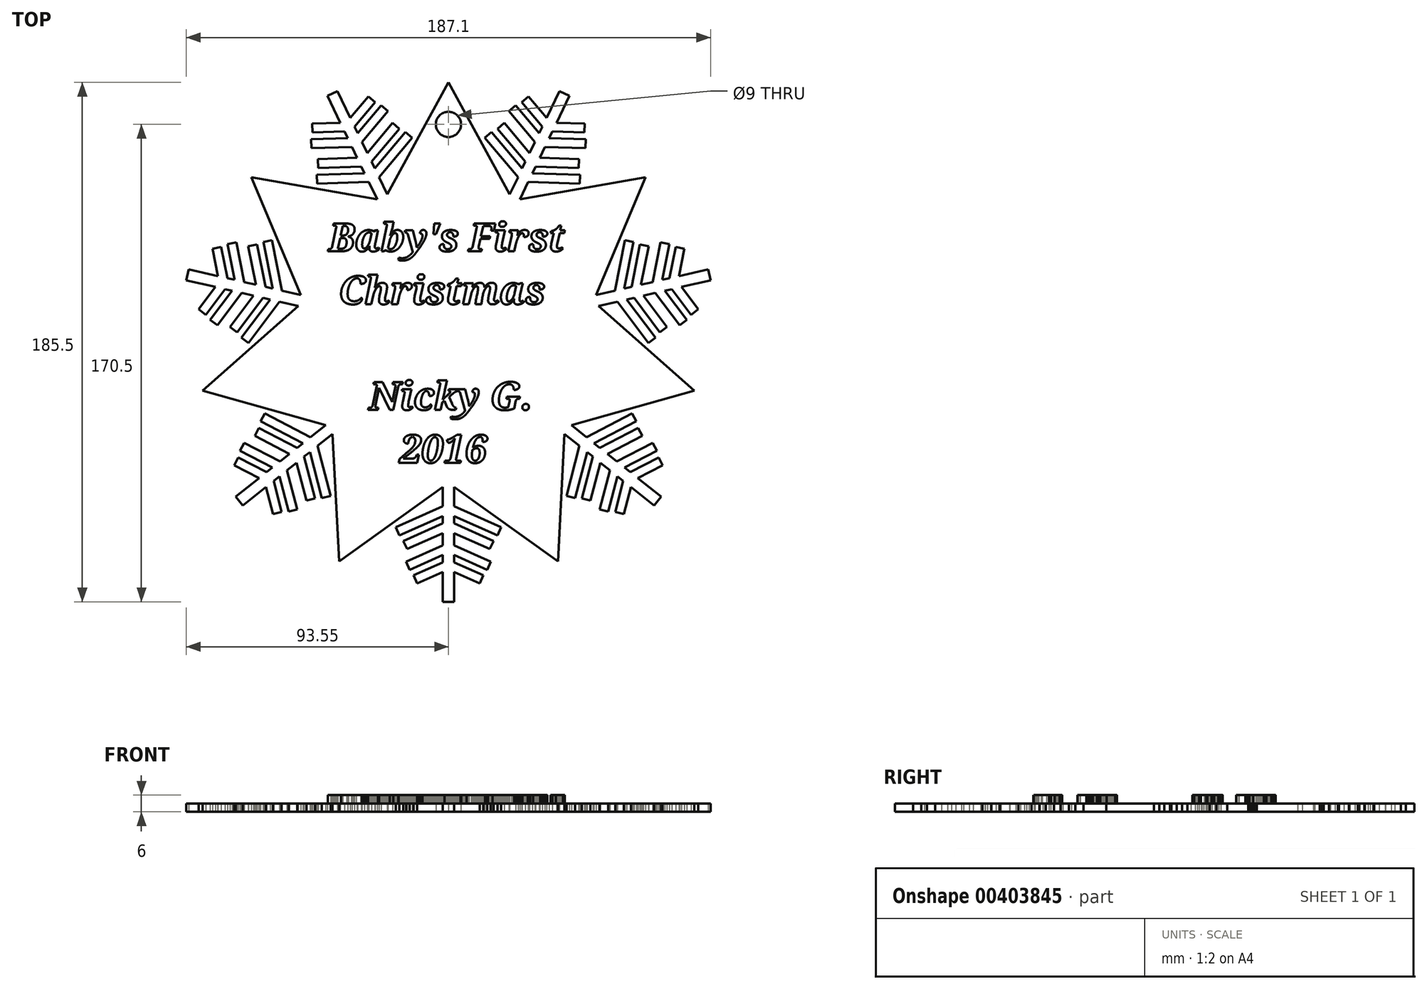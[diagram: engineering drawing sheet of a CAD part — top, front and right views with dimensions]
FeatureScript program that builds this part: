
annotation { "Feature Type Name" : "Feature", "Feature Type Description" : "" }
export const myFeature = defineFeature(function(context is Context, id is Id, definition is map)
    precondition{}
    {
        {
            var Q0;
            Q0=qCreatedBy(makeId("Top.planeOp"),FACE);
            var sketch = newSketch(context, id + "F0", { "sketchPlane" : qUnion([Q0])});
            skLineSegment(sketch, "E0.0", {"start": v(-21.86, 50) * mm, "end": v(21.86, 50) * mm});
            skLineSegment(sketch, "E0.1", {"start": v(25.46, 48.26) * mm, "end": v(52.72, 14.08) * mm});
            skLineSegment(sketch, "E0.2", {"start": v(53.61, 10.18) * mm, "end": v(43.88, -32.44) * mm});
            skLineSegment(sketch, "E0.3", {"start": v(41.39, -35.56) * mm, "end": v(2, -54.53) * mm});
            skLineSegment(sketch, "E0.4", {"start": v(-2, -54.53) * mm, "end": v(-41.39, -35.56) * mm});
            skLineSegment(sketch, "E0.5", {"start": v(-43.88, -32.44) * mm, "end": v(-53.61, 10.18) * mm});
            skLineSegment(sketch, "E0.6", {"start": v(-52.72, 14.08) * mm, "end": v(-25.46, 48.26) * mm});
            skPoint(sketch, "E0.0.midPoint", {"position": v(0, 50) * mm});
            skLineSegment(sketch, "E1", {"start": v(0, 0) * mm, "end": v(24.08, 50) * mm, "construction": true});
            skLineSegment(sketch, "E2", {"start": v(0, 0) * mm, "end": v(-24.08, 50) * mm, "construction": true});
            skLineSegment(sketch, "E3", {"start": v(0, 0) * mm, "end": v(-54.1, 12.35) * mm, "construction": true});
            skLineSegment(sketch, "E4", {"start": v(0, 0) * mm, "end": v(-43.39, -34.6) * mm, "construction": true});
            skLineSegment(sketch, "E5", {"start": v(0, 0) * mm, "end": v(0, -55.5) * mm, "construction": true});
            skLineSegment(sketch, "E6", {"start": v(0, 0) * mm, "end": v(43.39, -34.6) * mm, "construction": true});
            skLineSegment(sketch, "E7", {"start": v(0, 0) * mm, "end": v(54.1, 12.35) * mm, "construction": true});
            skLineSegment(sketch, "E8", {"start": v(-24.08, 50) * mm, "end": v(-41.43, 86.04) * mm, "construction": true});
            skLineSegment(sketch, "E9", {"start": v(24.08, 50) * mm, "end": v(41.43, 86.04) * mm, "construction": true});
            skLineSegment(sketch, "E10", {"start": v(54.1, 12.35) * mm, "end": v(93.1, 21.25) * mm, "construction": true});
            skLineSegment(sketch, "E11", {"start": v(43.39, -34.6) * mm, "end": v(74.66, -59.54) * mm, "construction": true});
            skLineSegment(sketch, "E12", {"start": v(0, -55.5) * mm, "end": v(0, -95.5) * mm, "construction": true});
            skLineSegment(sketch, "E13", {"start": v(-43.39, -34.6) * mm, "end": v(-74.66, -59.54) * mm, "construction": true});
            skLineSegment(sketch, "E14.0", {"start": v(-25.88, 49.13) * mm, "end": v(-28.43, 54.43) * mm});
            skLineSegment(sketch, "E15.0", {"start": v(25.88, 49.13) * mm, "end": v(28.43, 54.43) * mm});
            skLineSegment(sketch, "E16.0", {"start": v(54.55, 10.4) * mm, "end": v(60.28, 11.7) * mm});
            skLineSegment(sketch, "E17.0", {"start": v(53.66, 14.3) * mm, "end": v(59.39, 15.6) * mm});
            skLineSegment(sketch, "E18.0", {"start": v(42.14, -36.16) * mm, "end": v(46.74, -39.83) * mm});
            skLineSegment(sketch, "E19.0", {"start": v(44.64, -33.04) * mm, "end": v(49.23, -36.7) * mm});
            skLineSegment(sketch, "E20.0", {"start": v(2, -55.5) * mm, "end": v(2, -61.37) * mm});
            skLineSegment(sketch, "E21.0", {"start": v(-2, -55.5) * mm, "end": v(-2, -61.37) * mm});
            skLineSegment(sketch, "E22.0", {"start": v(-44.64, -33.04) * mm, "end": v(-49.23, -36.7) * mm});
            skLineSegment(sketch, "E23.0", {"start": v(-42.14, -36.16) * mm, "end": v(-46.74, -39.83) * mm});
            skLineSegment(sketch, "E24.0", {"start": v(-53.66, 14.3) * mm, "end": v(-59.39, 15.6) * mm});
            skLineSegment(sketch, "E25.0", {"start": v(-54.55, 10.4) * mm, "end": v(-60.28, 11.7) * mm});
            skLineSegment(sketch, "E26", {"start": v(-22.28, 50.87) * mm, "end": v(-21.86, 50) * mm});
            skLineSegment(sketch, "E27", {"start": v(-25.88, 49.13) * mm, "end": v(-25.46, 48.26) * mm});
            skLineSegment(sketch, "E28", {"start": v(-53.66, 14.3) * mm, "end": v(-52.72, 14.08) * mm});
            skLineSegment(sketch, "E29", {"start": v(-54.55, 10.4) * mm, "end": v(-53.61, 10.18) * mm});
            skLineSegment(sketch, "E30", {"start": v(-44.64, -33.04) * mm, "end": v(-43.88, -32.44) * mm});
            skLineSegment(sketch, "E31", {"start": v(-42.14, -36.16) * mm, "end": v(-41.39, -35.56) * mm});
            skLineSegment(sketch, "E32", {"start": v(-2, -55.5) * mm, "end": v(-2, -54.53) * mm});
            skLineSegment(sketch, "E33", {"start": v(2, -55.5) * mm, "end": v(2, -54.53) * mm});
            skLineSegment(sketch, "E34", {"start": v(42.14, -36.16) * mm, "end": v(41.39, -35.56) * mm});
            skLineSegment(sketch, "E35", {"start": v(44.64, -33.04) * mm, "end": v(43.88, -32.44) * mm});
            skLineSegment(sketch, "E36", {"start": v(54.55, 10.4) * mm, "end": v(53.61, 10.18) * mm});
            skLineSegment(sketch, "E37", {"start": v(53.66, 14.3) * mm, "end": v(52.72, 14.08) * mm});
            skLineSegment(sketch, "E38", {"start": v(22.28, 50.87) * mm, "end": v(21.86, 50) * mm});
            skLineSegment(sketch, "E39", {"start": v(25.88, 49.13) * mm, "end": v(25.46, 48.26) * mm});
            skLineSegment(sketch, "E40", {"start": v(-43.24, 85.17) * mm, "end": v(-39.63, 86.9) * mm});
            skLineSegment(sketch, "E41", {"start": v(43.24, 85.17) * mm, "end": v(39.63, 86.9) * mm});
            skLineSegment(sketch, "E42", {"start": v(93.55, 19.3) * mm, "end": v(92.66, 23.2) * mm});
            skLineSegment(sketch, "E43", {"start": v(73.41, -61.1) * mm, "end": v(75.9, -57.98) * mm});
            skLineSegment(sketch, "E44", {"start": v(2, -95.5) * mm, "end": v(-2, -95.5) * mm});
            skLineSegment(sketch, "E45", {"start": v(-73.41, -61.1) * mm, "end": v(-75.9, -57.98) * mm});
            skLineSegment(sketch, "E46", {"start": v(-93.55, 19.3) * mm, "end": v(-92.66, 23.2) * mm});
            skPoint(sketch, "E47.6.1", {"position": v(-40.06, 76.4) * mm});
            skPoint(sketch, "E47.6.2", {"position": v(-39.8, 73.96) * mm});
            skPoint(sketch, "E47.6.14", {"position": v(-34.76, 78.96) * mm});
            skPoint(sketch, "E47.6.19", {"position": v(-33.01, 77.23) * mm});
            skPoint(sketch, "E47.center", {"position": v(0, 0) * mm});
            skLineSegment(sketch, "E48.trimOffspring", {"start": v(-82.3, 20.84) * mm, "end": v(-92.66, 23.2) * mm});
            skLineSegment(sketch, "E49.trimOffspring", {"start": v(-76.35, 19.48) * mm, "end": v(-78.9, 20.06) * mm});
            skLineSegment(sketch, "E50.trimOffspring", {"start": v(-68.74, 17.74) * mm, "end": v(-72.95, 18.7) * mm});
            skLineSegment(sketch, "E51.trimOffspring", {"start": v(-62.79, 16.38) * mm, "end": v(-65.34, 16.96) * mm});
            skLineSegment(sketch, "E52.trimOffspring", {"start": v(-63.68, 12.48) * mm, "end": v(-66.23, 13.06) * mm});
            skLineSegment(sketch, "E53.trimOffspring", {"start": v(-69.63, 13.84) * mm, "end": v(-73.84, 14.8) * mm});
            skLineSegment(sketch, "E54.trimOffspring", {"start": v(-83.2, 16.94) * mm, "end": v(-93.55, 19.3) * mm});
            skLineSegment(sketch, "E55.trimOffspring", {"start": v(-77.24, 15.58) * mm, "end": v(-79.8, 16.16) * mm});
            skLineSegment(sketch, "E56.trimOffspring", {"start": v(-26.34, 59.3) * mm, "end": v(-27.47, 61.66) * mm});
            skLineSegment(sketch, "E57.trimOffspring", {"start": v(-29.94, 57.57) * mm, "end": v(-31.08, 59.93) * mm});
            skLineSegment(sketch, "E58.trimOffspring", {"start": v(-35.98, 70.1) * mm, "end": v(-37.11, 72.46) * mm});
            skLineSegment(sketch, "E59.trimOffspring", {"start": v(-35.02, 77.34) * mm, "end": v(-39.63, 86.9) * mm});
            skLineSegment(sketch, "E60.trimOffspring", {"start": v(-32.38, 71.84) * mm, "end": v(-33.51, 74.2) * mm});
            skLineSegment(sketch, "E61.trimOffspring", {"start": v(-28.99, 64.8) * mm, "end": v(-30.86, 68.7) * mm});
            skLineSegment(sketch, "E62.trimOffspring", {"start": v(-38.63, 75.6) * mm, "end": v(-43.24, 85.17) * mm});
            skLineSegment(sketch, "E63.trimOffspring", {"start": v(29.94, 57.57) * mm, "end": v(31.08, 59.93) * mm});
            skLineSegment(sketch, "E64.trimOffspring", {"start": v(26.34, 59.3) * mm, "end": v(27.47, 61.66) * mm});
            skLineSegment(sketch, "E65.trimOffspring", {"start": v(28.99, 64.8) * mm, "end": v(30.86, 68.7) * mm});
            skLineSegment(sketch, "E66.trimOffspring", {"start": v(32.38, 71.84) * mm, "end": v(33.51, 74.2) * mm});
            skLineSegment(sketch, "E67.trimOffspring", {"start": v(35.98, 70.1) * mm, "end": v(37.11, 72.46) * mm});
            skLineSegment(sketch, "E68.trimOffspring", {"start": v(35.02, 77.34) * mm, "end": v(39.63, 86.9) * mm});
            skLineSegment(sketch, "E69.trimOffspring", {"start": v(38.63, 75.6) * mm, "end": v(43.24, 85.17) * mm});
            skLineSegment(sketch, "E70.trimOffspring", {"start": v(63.68, 12.48) * mm, "end": v(66.23, 13.06) * mm});
            skLineSegment(sketch, "E71.trimOffspring", {"start": v(62.79, 16.38) * mm, "end": v(65.34, 16.96) * mm});
            skLineSegment(sketch, "E72.trimOffspring", {"start": v(69.63, 13.84) * mm, "end": v(73.84, 14.8) * mm});
            skLineSegment(sketch, "E73.trimOffspring", {"start": v(68.74, 17.74) * mm, "end": v(72.95, 18.7) * mm});
            skLineSegment(sketch, "E74.trimOffspring", {"start": v(77.24, 15.58) * mm, "end": v(79.8, 16.16) * mm});
            skLineSegment(sketch, "E75.trimOffspring", {"start": v(76.35, 19.48) * mm, "end": v(78.9, 20.06) * mm});
            skLineSegment(sketch, "E76.trimOffspring", {"start": v(82.3, 20.84) * mm, "end": v(92.66, 23.2) * mm});
            skLineSegment(sketch, "E77.trimOffspring", {"start": v(83.2, 16.94) * mm, "end": v(93.55, 19.3) * mm});
            skLineSegment(sketch, "E78.trimOffspring", {"start": v(65.1, -54.48) * mm, "end": v(73.41, -61.1) * mm});
            skLineSegment(sketch, "E79.trimOffspring", {"start": v(67.6, -51.35) * mm, "end": v(75.9, -57.98) * mm});
            skLineSegment(sketch, "E80.trimOffspring", {"start": v(62.83, -47.55) * mm, "end": v(64.88, -49.18) * mm});
            skLineSegment(sketch, "E81.trimOffspring", {"start": v(60.34, -50.68) * mm, "end": v(62.38, -52.3) * mm});
            skLineSegment(sketch, "E82.trimOffspring", {"start": v(54.23, -45.8) * mm, "end": v(57.61, -48.5) * mm});
            skLineSegment(sketch, "E83.trimOffspring", {"start": v(56.73, -42.68) * mm, "end": v(60.1, -45.38) * mm});
            skLineSegment(sketch, "E84.trimOffspring", {"start": v(51.96, -38.88) * mm, "end": v(54, -40.5) * mm});
            skLineSegment(sketch, "E85.trimOffspring", {"start": v(49.46, -42) * mm, "end": v(51.5, -43.63) * mm});
            skLineSegment(sketch, "E86.trimOffspring", {"start": v(-2, -84.87) * mm, "end": v(-2, -95.5) * mm});
            skLineSegment(sketch, "E87.trimOffspring", {"start": v(2, -84.87) * mm, "end": v(2, -95.5) * mm});
            skLineSegment(sketch, "E88.trimOffspring", {"start": v(2, -78.77) * mm, "end": v(2, -81.39) * mm});
            skLineSegment(sketch, "E89.trimOffspring", {"start": v(-2, -78.77) * mm, "end": v(-2, -81.39) * mm});
            skLineSegment(sketch, "E90.trimOffspring", {"start": v(-2, -70.96) * mm, "end": v(-2, -75.28) * mm});
            skLineSegment(sketch, "E91.trimOffspring", {"start": v(2, -70.96) * mm, "end": v(2, -75.28) * mm});
            skLineSegment(sketch, "E92.trimOffspring", {"start": v(2, -64.86) * mm, "end": v(2, -67.48) * mm});
            skLineSegment(sketch, "E93.trimOffspring", {"start": v(-2, -64.86) * mm, "end": v(-2, -67.48) * mm});
            skLineSegment(sketch, "E94.trimOffspring", {"start": v(-67.6, -51.35) * mm, "end": v(-75.9, -57.98) * mm});
            skLineSegment(sketch, "E95.trimOffspring", {"start": v(-65.1, -54.48) * mm, "end": v(-73.41, -61.1) * mm});
            skLineSegment(sketch, "E96.trimOffspring", {"start": v(-60.34, -50.68) * mm, "end": v(-62.38, -52.3) * mm});
            skLineSegment(sketch, "E97.trimOffspring", {"start": v(-62.83, -47.55) * mm, "end": v(-64.88, -49.18) * mm});
            skLineSegment(sketch, "E98.trimOffspring", {"start": v(-56.73, -42.68) * mm, "end": v(-60.1, -45.38) * mm});
            skLineSegment(sketch, "E99.trimOffspring", {"start": v(-54.23, -45.8) * mm, "end": v(-57.61, -48.5) * mm});
            skLineSegment(sketch, "E100.trimOffspring", {"start": v(-49.46, -42) * mm, "end": v(-51.5, -43.63) * mm});
            skLineSegment(sketch, "E101.trimOffspring", {"start": v(-51.96, -38.88) * mm, "end": v(-54, -40.5) * mm});
            skLineSegment(sketch, "E102", {"start": v(-24.83, 56.16) * mm, "end": v(-22.28, 50.87) * mm});
            skLineSegment(sketch, "E103", {"start": v(24.83, 56.16) * mm, "end": v(22.28, 50.87) * mm});
            skLineSegment(sketch, "E104", {"start": v(-34.47, 66.96) * mm, "end": v(-32.6, 63.07) * mm});
            skLineSegment(sketch, "E105", {"start": v(34.47, 66.96) * mm, "end": v(32.6, 63.07) * mm});
            skLineSegment(sketch, "E106", {"start": v(79.8, 16.16) * mm, "end": v(86.64, 7.02) * mm});
            skLineSegment(sketch, "E107", {"start": v(83.2, 16.94) * mm, "end": v(89.19, 8.93) * mm});
            skLineSegment(sketch, "E108", {"start": v(86.64, 7.02) * mm, "end": v(89.19, 8.93) * mm});
            skLineSegment(sketch, "E109", {"start": v(77.24, 15.58) * mm, "end": v(85.04, 5.18) * mm});
            skLineSegment(sketch, "E110", {"start": v(73.84, 14.8) * mm, "end": v(82.5, 3.27) * mm});
            skLineSegment(sketch, "E111", {"start": v(85.04, 5.18) * mm, "end": v(82.5, 3.27) * mm});
            skLineSegment(sketch, "E112", {"start": v(69.63, 13.84) * mm, "end": v(78.03, 2.64) * mm});
            skLineSegment(sketch, "E113", {"start": v(66.23, 13.06) * mm, "end": v(75.48, 0.73) * mm});
            skLineSegment(sketch, "E114", {"start": v(78.03, 2.64) * mm, "end": v(75.48, 0.73) * mm});
            skLineSegment(sketch, "E115", {"start": v(63.68, 12.48) * mm, "end": v(73.88, -1.12) * mm});
            skLineSegment(sketch, "E116", {"start": v(60.28, 11.7) * mm, "end": v(71.33, -3.03) * mm});
            skLineSegment(sketch, "E117", {"start": v(73.88, -1.12) * mm, "end": v(71.33, -3.03) * mm});
            skLineSegment(sketch, "E118.MirrorCS", {"start": v(71.44, 31.48) * mm, "end": v(68.32, 32.1) * mm});
            skLineSegment(sketch, "E119.MirrorCS", {"start": v(59.39, 15.6) * mm, "end": v(62.95, 33.68) * mm});
            skLineSegment(sketch, "E120.MirrorCS", {"start": v(66.07, 33.06) * mm, "end": v(62.95, 33.68) * mm});
            skLineSegment(sketch, "E121.MirrorCS", {"start": v(62.79, 16.38) * mm, "end": v(66.07, 33.06) * mm});
            skLineSegment(sketch, "E122.MirrorCS", {"start": v(65.34, 16.96) * mm, "end": v(68.32, 32.1) * mm});
            skLineSegment(sketch, "E123.MirrorCS", {"start": v(68.74, 17.74) * mm, "end": v(71.44, 31.48) * mm});
            skLineSegment(sketch, "E124.MirrorCS", {"start": v(72.95, 18.7) * mm, "end": v(75.74, 32.85) * mm});
            skLineSegment(sketch, "E125.MirrorCS", {"start": v(78.86, 32.23) * mm, "end": v(75.74, 32.85) * mm});
            skLineSegment(sketch, "E126.MirrorCS", {"start": v(76.35, 19.48) * mm, "end": v(78.86, 32.23) * mm});
            skLineSegment(sketch, "E127.MirrorCS", {"start": v(78.9, 20.06) * mm, "end": v(81.1, 31.26) * mm});
            skLineSegment(sketch, "E128.MirrorCS", {"start": v(82.3, 20.84) * mm, "end": v(84.23, 30.65) * mm});
            skLineSegment(sketch, "E129.MirrorCS", {"start": v(81.1, 31.26) * mm, "end": v(84.23, 30.65) * mm});
            skLineSegment(sketch, "E130.1.0", {"start": v(48.53, 72.12) * mm, "end": v(48.62, 75.3) * mm});
            skLineSegment(sketch, "E130.1.1", {"start": v(38.63, 75.6) * mm, "end": v(48.62, 75.3) * mm});
            skLineSegment(sketch, "E130.1.2", {"start": v(37.11, 72.46) * mm, "end": v(48.53, 72.12) * mm});
            skLineSegment(sketch, "E130.1.3", {"start": v(35.98, 70.1) * mm, "end": v(48.97, 69.71) * mm});
            skLineSegment(sketch, "E130.1.4", {"start": v(48.97, 69.71) * mm, "end": v(48.88, 66.53) * mm});
            skLineSegment(sketch, "E130.1.5", {"start": v(34.47, 66.96) * mm, "end": v(48.88, 66.53) * mm});
            skLineSegment(sketch, "E130.1.6", {"start": v(32.6, 63.07) * mm, "end": v(46.59, 62.65) * mm});
            skLineSegment(sketch, "E130.1.7", {"start": v(46.59, 62.65) * mm, "end": v(46.49, 59.46) * mm});
            skLineSegment(sketch, "E130.1.8", {"start": v(31.08, 59.93) * mm, "end": v(46.49, 59.46) * mm});
            skLineSegment(sketch, "E130.1.9", {"start": v(29.94, 57.57) * mm, "end": v(46.94, 57.06) * mm});
            skLineSegment(sketch, "E130.1.10", {"start": v(46.94, 57.06) * mm, "end": v(46.84, 53.88) * mm});
            skLineSegment(sketch, "E130.1.11", {"start": v(28.43, 54.43) * mm, "end": v(46.84, 53.88) * mm});
            skLineSegment(sketch, "E130.1.12", {"start": v(24.83, 56.16) * mm, "end": v(12.92, 70.21) * mm});
            skLineSegment(sketch, "E130.1.13", {"start": v(26.34, 59.3) * mm, "end": v(15.35, 72.27) * mm});
            skLineSegment(sketch, "E130.1.14", {"start": v(27.47, 61.66) * mm, "end": v(17.5, 73.42) * mm});
            skLineSegment(sketch, "E130.1.15", {"start": v(28.99, 64.8) * mm, "end": v(19.94, 75.48) * mm});
            skLineSegment(sketch, "E130.1.16", {"start": v(30.86, 68.7) * mm, "end": v(21.54, 79.7) * mm});
            skLineSegment(sketch, "E130.1.17", {"start": v(32.38, 71.84) * mm, "end": v(23.97, 81.75) * mm});
            skLineSegment(sketch, "E130.1.18", {"start": v(33.51, 74.2) * mm, "end": v(26.13, 82.9) * mm});
            skLineSegment(sketch, "E130.1.19", {"start": v(35.02, 77.34) * mm, "end": v(28.56, 84.96) * mm});
            skLineSegment(sketch, "E130.1.20", {"start": v(26.13, 82.9) * mm, "end": v(28.56, 84.96) * mm});
            skLineSegment(sketch, "E130.1.21", {"start": v(23.97, 81.75) * mm, "end": v(21.54, 79.7) * mm});
            skLineSegment(sketch, "E130.1.22", {"start": v(19.94, 75.48) * mm, "end": v(17.5, 73.42) * mm});
            skLineSegment(sketch, "E130.1.23", {"start": v(15.35, 72.27) * mm, "end": v(12.92, 70.21) * mm});
            skLineSegment(sketch, "E130.2.0", {"start": v(-26.13, 82.9) * mm, "end": v(-28.56, 84.96) * mm});
            skLineSegment(sketch, "E130.2.1", {"start": v(-35.02, 77.34) * mm, "end": v(-28.56, 84.96) * mm});
            skLineSegment(sketch, "E130.2.2", {"start": v(-33.51, 74.2) * mm, "end": v(-26.13, 82.9) * mm});
            skLineSegment(sketch, "E130.2.3", {"start": v(-32.38, 71.84) * mm, "end": v(-23.97, 81.75) * mm});
            skLineSegment(sketch, "E130.2.4", {"start": v(-23.97, 81.75) * mm, "end": v(-21.54, 79.7) * mm});
            skLineSegment(sketch, "E130.2.5", {"start": v(-30.86, 68.7) * mm, "end": v(-21.54, 79.7) * mm});
            skLineSegment(sketch, "E130.2.6", {"start": v(-28.99, 64.8) * mm, "end": v(-19.94, 75.48) * mm});
            skLineSegment(sketch, "E130.2.7", {"start": v(-19.94, 75.48) * mm, "end": v(-17.5, 73.42) * mm});
            skLineSegment(sketch, "E130.2.8", {"start": v(-27.47, 61.66) * mm, "end": v(-17.5, 73.42) * mm});
            skLineSegment(sketch, "E130.2.9", {"start": v(-26.34, 59.3) * mm, "end": v(-15.35, 72.27) * mm});
            skLineSegment(sketch, "E130.2.10", {"start": v(-15.35, 72.27) * mm, "end": v(-12.92, 70.21) * mm});
            skLineSegment(sketch, "E130.2.11", {"start": v(-24.83, 56.16) * mm, "end": v(-12.92, 70.21) * mm});
            skLineSegment(sketch, "E130.2.12", {"start": v(-28.43, 54.43) * mm, "end": v(-46.84, 53.88) * mm});
            skLineSegment(sketch, "E130.2.13", {"start": v(-29.94, 57.57) * mm, "end": v(-46.94, 57.06) * mm});
            skLineSegment(sketch, "E130.2.14", {"start": v(-31.08, 59.93) * mm, "end": v(-46.49, 59.46) * mm});
            skLineSegment(sketch, "E130.2.15", {"start": v(-32.6, 63.07) * mm, "end": v(-46.59, 62.65) * mm});
            skLineSegment(sketch, "E130.2.16", {"start": v(-34.47, 66.96) * mm, "end": v(-48.88, 66.53) * mm});
            skLineSegment(sketch, "E130.2.17", {"start": v(-35.98, 70.1) * mm, "end": v(-48.97, 69.71) * mm});
            skLineSegment(sketch, "E130.2.18", {"start": v(-37.11, 72.46) * mm, "end": v(-48.53, 72.12) * mm});
            skLineSegment(sketch, "E130.2.19", {"start": v(-38.63, 75.6) * mm, "end": v(-48.62, 75.3) * mm});
            skLineSegment(sketch, "E130.2.20", {"start": v(-48.53, 72.12) * mm, "end": v(-48.62, 75.3) * mm});
            skLineSegment(sketch, "E130.2.21", {"start": v(-48.97, 69.71) * mm, "end": v(-48.88, 66.53) * mm});
            skLineSegment(sketch, "E130.2.22", {"start": v(-46.59, 62.65) * mm, "end": v(-46.49, 59.46) * mm});
            skLineSegment(sketch, "E130.2.23", {"start": v(-46.94, 57.06) * mm, "end": v(-46.84, 53.88) * mm});
            skLineSegment(sketch, "E130.3.0", {"start": v(-81.1, 31.26) * mm, "end": v(-84.23, 30.65) * mm});
            skLineSegment(sketch, "E130.3.1", {"start": v(-82.3, 20.84) * mm, "end": v(-84.23, 30.65) * mm});
            skLineSegment(sketch, "E130.3.2", {"start": v(-78.9, 20.06) * mm, "end": v(-81.1, 31.26) * mm});
            skLineSegment(sketch, "E130.3.3", {"start": v(-76.35, 19.48) * mm, "end": v(-78.86, 32.23) * mm});
            skLineSegment(sketch, "E130.3.4", {"start": v(-78.86, 32.23) * mm, "end": v(-75.74, 32.85) * mm});
            skLineSegment(sketch, "E130.3.5", {"start": v(-72.95, 18.7) * mm, "end": v(-75.74, 32.85) * mm});
            skLineSegment(sketch, "E130.3.6", {"start": v(-68.74, 17.74) * mm, "end": v(-71.44, 31.48) * mm});
            skLineSegment(sketch, "E130.3.7", {"start": v(-71.44, 31.48) * mm, "end": v(-68.32, 32.1) * mm});
            skLineSegment(sketch, "E130.3.8", {"start": v(-65.34, 16.96) * mm, "end": v(-68.32, 32.1) * mm});
            skLineSegment(sketch, "E130.3.9", {"start": v(-62.79, 16.38) * mm, "end": v(-66.07, 33.06) * mm});
            skLineSegment(sketch, "E130.3.10", {"start": v(-66.07, 33.06) * mm, "end": v(-62.95, 33.68) * mm});
            skLineSegment(sketch, "E130.3.11", {"start": v(-59.39, 15.6) * mm, "end": v(-62.95, 33.68) * mm});
            skLineSegment(sketch, "E130.3.12", {"start": v(-60.28, 11.7) * mm, "end": v(-71.33, -3.03) * mm});
            skLineSegment(sketch, "E130.3.13", {"start": v(-63.68, 12.48) * mm, "end": v(-73.88, -1.12) * mm});
            skLineSegment(sketch, "E130.3.14", {"start": v(-66.23, 13.06) * mm, "end": v(-75.48, 0.73) * mm});
            skLineSegment(sketch, "E130.3.15", {"start": v(-69.63, 13.84) * mm, "end": v(-78.03, 2.64) * mm});
            skLineSegment(sketch, "E130.3.16", {"start": v(-73.84, 14.8) * mm, "end": v(-82.5, 3.27) * mm});
            skLineSegment(sketch, "E130.3.17", {"start": v(-77.24, 15.58) * mm, "end": v(-85.04, 5.18) * mm});
            skLineSegment(sketch, "E130.3.18", {"start": v(-79.8, 16.16) * mm, "end": v(-86.64, 7.02) * mm});
            skLineSegment(sketch, "E130.3.19", {"start": v(-83.2, 16.94) * mm, "end": v(-89.19, 8.93) * mm});
            skLineSegment(sketch, "E130.3.20", {"start": v(-86.64, 7.02) * mm, "end": v(-89.19, 8.93) * mm});
            skLineSegment(sketch, "E130.3.21", {"start": v(-85.04, 5.18) * mm, "end": v(-82.5, 3.27) * mm});
            skLineSegment(sketch, "E130.3.22", {"start": v(-78.03, 2.64) * mm, "end": v(-75.48, 0.73) * mm});
            skLineSegment(sketch, "E130.3.23", {"start": v(-73.88, -1.12) * mm, "end": v(-71.33, -3.03) * mm});
            skLineSegment(sketch, "E130.4.0", {"start": v(-75.01, -43.92) * mm, "end": v(-76.48, -46.75) * mm});
            skLineSegment(sketch, "E130.4.1", {"start": v(-67.6, -51.35) * mm, "end": v(-76.48, -46.75) * mm});
            skLineSegment(sketch, "E130.4.2", {"start": v(-64.88, -49.18) * mm, "end": v(-75.01, -43.92) * mm});
            skLineSegment(sketch, "E130.4.3", {"start": v(-62.83, -47.55) * mm, "end": v(-74.37, -41.56) * mm});
            skLineSegment(sketch, "E130.4.4", {"start": v(-74.37, -41.56) * mm, "end": v(-72.9, -38.73) * mm});
            skLineSegment(sketch, "E130.4.5", {"start": v(-60.1, -45.38) * mm, "end": v(-72.9, -38.73) * mm});
            skLineSegment(sketch, "E130.4.6", {"start": v(-56.73, -42.68) * mm, "end": v(-69.15, -36.23) * mm});
            skLineSegment(sketch, "E130.4.7", {"start": v(-69.15, -36.23) * mm, "end": v(-67.69, -33.4) * mm});
            skLineSegment(sketch, "E130.4.8", {"start": v(-54, -40.5) * mm, "end": v(-67.69, -33.4) * mm});
            skLineSegment(sketch, "E130.4.9", {"start": v(-51.96, -38.88) * mm, "end": v(-67.05, -31.05) * mm});
            skLineSegment(sketch, "E130.4.10", {"start": v(-67.05, -31.05) * mm, "end": v(-65.58, -28.22) * mm});
            skLineSegment(sketch, "E130.4.11", {"start": v(-49.23, -36.7) * mm, "end": v(-65.58, -28.22) * mm});
            skLineSegment(sketch, "E130.4.12", {"start": v(-46.74, -39.83) * mm, "end": v(-42.1, -57.66) * mm});
            skLineSegment(sketch, "E130.4.13", {"start": v(-49.46, -42) * mm, "end": v(-45.19, -58.46) * mm});
            skLineSegment(sketch, "E130.4.14", {"start": v(-51.5, -43.63) * mm, "end": v(-47.63, -58.56) * mm});
            skLineSegment(sketch, "E130.4.15", {"start": v(-54.23, -45.8) * mm, "end": v(-50.71, -59.36) * mm});
            skLineSegment(sketch, "E130.4.16", {"start": v(-57.61, -48.5) * mm, "end": v(-53.99, -62.46) * mm});
            skLineSegment(sketch, "E130.4.17", {"start": v(-60.34, -50.68) * mm, "end": v(-57.07, -63.26) * mm});
            skLineSegment(sketch, "E130.4.18", {"start": v(-62.38, -52.3) * mm, "end": v(-59.51, -63.36) * mm});
            skLineSegment(sketch, "E130.4.19", {"start": v(-65.1, -54.48) * mm, "end": v(-62.6, -64.16) * mm});
            skLineSegment(sketch, "E130.4.20", {"start": v(-59.51, -63.36) * mm, "end": v(-62.6, -64.16) * mm});
            skLineSegment(sketch, "E130.4.21", {"start": v(-57.07, -63.26) * mm, "end": v(-53.99, -62.46) * mm});
            skLineSegment(sketch, "E130.4.22", {"start": v(-50.71, -59.36) * mm, "end": v(-47.63, -58.56) * mm});
            skLineSegment(sketch, "E130.4.23", {"start": v(-45.19, -58.46) * mm, "end": v(-42.1, -57.66) * mm});
            skLineSegment(sketch, "E130.5.0", {"start": v(-12.43, -86.03) * mm, "end": v(-11.14, -88.94) * mm});
            skLineSegment(sketch, "E130.5.1", {"start": v(-2, -84.87) * mm, "end": v(-11.14, -88.94) * mm});
            skLineSegment(sketch, "E130.5.2", {"start": v(-2, -81.39) * mm, "end": v(-12.43, -86.03) * mm});
            skLineSegment(sketch, "E130.5.3", {"start": v(-2, -78.77) * mm, "end": v(-13.88, -84.06) * mm});
            skLineSegment(sketch, "E130.5.4", {"start": v(-13.88, -84.06) * mm, "end": v(-15.17, -81.15) * mm});
            skLineSegment(sketch, "E130.5.5", {"start": v(-2, -75.28) * mm, "end": v(-15.17, -81.15) * mm});
            skLineSegment(sketch, "E130.5.6", {"start": v(-2, -70.96) * mm, "end": v(-14.79, -76.66) * mm});
            skLineSegment(sketch, "E130.5.7", {"start": v(-14.79, -76.66) * mm, "end": v(-16.09, -73.75) * mm});
            skLineSegment(sketch, "E130.5.8", {"start": v(-2, -67.48) * mm, "end": v(-16.09, -73.75) * mm});
            skLineSegment(sketch, "E130.5.9", {"start": v(-2, -64.86) * mm, "end": v(-17.53, -71.78) * mm});
            skLineSegment(sketch, "E130.5.10", {"start": v(-17.53, -71.78) * mm, "end": v(-18.83, -68.87) * mm});
            skLineSegment(sketch, "E130.5.11", {"start": v(-2, -61.37) * mm, "end": v(-18.83, -68.87) * mm});
            skLineSegment(sketch, "E130.5.12", {"start": v(2, -61.37) * mm, "end": v(18.83, -68.87) * mm});
            skLineSegment(sketch, "E130.5.13", {"start": v(2, -64.86) * mm, "end": v(17.53, -71.78) * mm});
            skLineSegment(sketch, "E130.5.14", {"start": v(2, -67.48) * mm, "end": v(16.09, -73.75) * mm});
            skLineSegment(sketch, "E130.5.15", {"start": v(2, -70.96) * mm, "end": v(14.79, -76.66) * mm});
            skLineSegment(sketch, "E130.5.16", {"start": v(2, -75.28) * mm, "end": v(15.17, -81.15) * mm});
            skLineSegment(sketch, "E130.5.17", {"start": v(2, -78.77) * mm, "end": v(13.88, -84.06) * mm});
            skLineSegment(sketch, "E130.5.18", {"start": v(2, -81.39) * mm, "end": v(12.43, -86.03) * mm});
            skLineSegment(sketch, "E130.5.19", {"start": v(2, -84.87) * mm, "end": v(11.14, -88.94) * mm});
            skLineSegment(sketch, "E130.5.20", {"start": v(12.43, -86.03) * mm, "end": v(11.14, -88.94) * mm});
            skLineSegment(sketch, "E130.5.21", {"start": v(13.88, -84.06) * mm, "end": v(15.17, -81.15) * mm});
            skLineSegment(sketch, "E130.5.22", {"start": v(14.79, -76.66) * mm, "end": v(16.09, -73.75) * mm});
            skLineSegment(sketch, "E130.5.23", {"start": v(17.53, -71.78) * mm, "end": v(18.83, -68.87) * mm});
            skLineSegment(sketch, "E130.6.0", {"start": v(59.51, -63.36) * mm, "end": v(62.6, -64.16) * mm});
            skLineSegment(sketch, "E130.6.1", {"start": v(65.1, -54.48) * mm, "end": v(62.6, -64.16) * mm});
            skLineSegment(sketch, "E130.6.2", {"start": v(62.38, -52.3) * mm, "end": v(59.51, -63.36) * mm});
            skLineSegment(sketch, "E130.6.3", {"start": v(60.34, -50.68) * mm, "end": v(57.07, -63.26) * mm});
            skLineSegment(sketch, "E130.6.4", {"start": v(57.07, -63.26) * mm, "end": v(53.99, -62.46) * mm});
            skLineSegment(sketch, "E130.6.5", {"start": v(57.61, -48.5) * mm, "end": v(53.99, -62.46) * mm});
            skLineSegment(sketch, "E130.6.6", {"start": v(54.23, -45.8) * mm, "end": v(50.71, -59.36) * mm});
            skLineSegment(sketch, "E130.6.7", {"start": v(50.71, -59.36) * mm, "end": v(47.63, -58.56) * mm});
            skLineSegment(sketch, "E130.6.8", {"start": v(51.5, -43.63) * mm, "end": v(47.63, -58.56) * mm});
            skLineSegment(sketch, "E130.6.9", {"start": v(49.46, -42) * mm, "end": v(45.19, -58.46) * mm});
            skLineSegment(sketch, "E130.6.10", {"start": v(45.19, -58.46) * mm, "end": v(42.1, -57.66) * mm});
            skLineSegment(sketch, "E130.6.11", {"start": v(46.74, -39.83) * mm, "end": v(42.1, -57.66) * mm});
            skLineSegment(sketch, "E130.6.12", {"start": v(49.23, -36.7) * mm, "end": v(65.58, -28.22) * mm});
            skLineSegment(sketch, "E130.6.13", {"start": v(51.96, -38.88) * mm, "end": v(67.05, -31.05) * mm});
            skLineSegment(sketch, "E130.6.14", {"start": v(54, -40.5) * mm, "end": v(67.69, -33.4) * mm});
            skLineSegment(sketch, "E130.6.15", {"start": v(56.73, -42.68) * mm, "end": v(69.15, -36.23) * mm});
            skLineSegment(sketch, "E130.6.16", {"start": v(60.1, -45.38) * mm, "end": v(72.9, -38.73) * mm});
            skLineSegment(sketch, "E130.6.17", {"start": v(62.83, -47.55) * mm, "end": v(74.37, -41.56) * mm});
            skLineSegment(sketch, "E130.6.18", {"start": v(64.88, -49.18) * mm, "end": v(75.01, -43.92) * mm});
            skLineSegment(sketch, "E130.6.19", {"start": v(67.6, -51.35) * mm, "end": v(76.48, -46.75) * mm});
            skLineSegment(sketch, "E130.6.20", {"start": v(75.01, -43.92) * mm, "end": v(76.48, -46.75) * mm});
            skLineSegment(sketch, "E130.6.21", {"start": v(74.37, -41.56) * mm, "end": v(72.9, -38.73) * mm});
            skLineSegment(sketch, "E130.6.22", {"start": v(69.15, -36.23) * mm, "end": v(67.69, -33.4) * mm});
            skLineSegment(sketch, "E130.6.23", {"start": v(67.05, -31.05) * mm, "end": v(65.58, -28.22) * mm});
            skSolve(sketch);
        }
        {
            var Q0;
            Q0 = qSketchRegion(id + "F0", true);
            extrude(context, id + "F1", {"entities" : qUnion([Q0]), "depth" : 3 * mm});
        }
        {
            var Q0;
            Q0=qCreatedBy(makeId("Top.planeOp"),FACE);
            var sketch = newSketch(context, id + "F2", { "sketchPlane" : qUnion([Q0])});
            skLineSegment(sketch, "E131.0", {"start": v(-52.72, 14.08) * mm, "end": v(-25.46, 48.26) * mm});
            skLineSegment(sketch, "E132.0", {"start": v(-21.86, 50) * mm, "end": v(21.86, 50) * mm});
            skLineSegment(sketch, "E133.0", {"start": v(25.46, 48.26) * mm, "end": v(52.72, 14.08) * mm});
            skLineSegment(sketch, "E134.0", {"start": v(53.61, 10.18) * mm, "end": v(43.88, -32.44) * mm});
            skLineSegment(sketch, "E135.0", {"start": v(41.39, -35.56) * mm, "end": v(2, -54.53) * mm});
            skLineSegment(sketch, "E136.0", {"start": v(-2, -54.53) * mm, "end": v(-41.39, -35.56) * mm});
            skLineSegment(sketch, "E137.0", {"start": v(-43.88, -32.44) * mm, "end": v(-53.61, 10.18) * mm});
            skLineSegment(sketch, "E138", {"start": v(-48.75, -11.13) * mm, "end": v(-87.74, -20.03) * mm, "construction": true});
            skLineSegment(sketch, "E139", {"start": v(-43.88, -32.44) * mm, "end": v(-87.74, -20.03) * mm});
            skLineSegment(sketch, "E140", {"start": v(-87.74, -20.03) * mm, "end": v(-53.61, 10.18) * mm});
            skLineSegment(sketch, "E141.1.0", {"start": v(-39.05, -81.09) * mm, "end": v(-41.39, -35.56) * mm});
            skLineSegment(sketch, "E141.1.1", {"start": v(-2, -54.53) * mm, "end": v(-39.05, -81.09) * mm});
            skLineSegment(sketch, "E141.2.0", {"start": v(39.05, -81.09) * mm, "end": v(2, -54.53) * mm});
            skLineSegment(sketch, "E141.2.1", {"start": v(41.39, -35.56) * mm, "end": v(39.05, -81.09) * mm});
            skLineSegment(sketch, "E141.3.0", {"start": v(87.74, -20.03) * mm, "end": v(43.88, -32.44) * mm});
            skLineSegment(sketch, "E141.3.1", {"start": v(53.61, 10.18) * mm, "end": v(87.74, -20.03) * mm});
            skLineSegment(sketch, "E141.4.0", {"start": v(70.36, 56.11) * mm, "end": v(52.72, 14.08) * mm});
            skLineSegment(sketch, "E141.4.1", {"start": v(25.46, 48.26) * mm, "end": v(70.36, 56.11) * mm});
            skLineSegment(sketch, "E141.5.0", {"start": v(0, 90) * mm, "end": v(21.86, 50) * mm});
            skLineSegment(sketch, "E141.5.1", {"start": v(-21.86, 50) * mm, "end": v(0, 90) * mm});
            skLineSegment(sketch, "E141.6.0", {"start": v(-70.36, 56.11) * mm, "end": v(-25.46, 48.26) * mm});
            skLineSegment(sketch, "E141.6.1", {"start": v(-52.72, 14.08) * mm, "end": v(-70.36, 56.11) * mm});
            skPoint(sketch, "E141.center", {"position": v(0, 0) * mm});
            skCircle(sketch, "E142", {"center": v(0, 75) * mm, "radius": 4.5 * mm});
            skSolve(sketch);
        }
        {
            var Q0;
            Q0 = qSketchRegion(id + "F2", true);
            extrude(context, id + "F3", {"entities" : qUnion([Q0]), "operationType" : NewBodyOperationType.ADD, "depth" : 3 * mm});
        }
        {
            var Q0;
            Q0=makeQuery(id+"F3.boolean.opBoolean","MERGE",FACE,{"derivedFrom":[makeQuery(id+"F1.opExtrude","CAP_FACE",FACE,{"disambiguationData":[OSD([sQuery(id+"F0.wireOp",EDGE,"E0.0"),sQuery(id+"F0.wireOp",EDGE,"E0.1"),sQuery(id+"F0.wireOp",EDGE,"E0.2"),sQuery(id+"F0.wireOp",EDGE,"E0.3"),sQuery(id+"F0.wireOp",EDGE,"E0.4"),sQuery(id+"F0.wireOp",EDGE,"E0.5"),sQuery(id+"F0.wireOp",EDGE,"E0.6"),sQuery(id+"F0.wireOp",EDGE,"E14.0"),sQuery(id+"F0.wireOp",EDGE,"E15.0"),sQuery(id+"F0.wireOp",EDGE,"E16.0"),sQuery(id+"F0.wireOp",EDGE,"E17.0"),sQuery(id+"F0.wireOp",EDGE,"E18.0"),sQuery(id+"F0.wireOp",EDGE,"E19.0"),sQuery(id+"F0.wireOp",EDGE,"E20.0"),sQuery(id+"F0.wireOp",EDGE,"E21.0"),sQuery(id+"F0.wireOp",EDGE,"E22.0"),sQuery(id+"F0.wireOp",EDGE,"E23.0"),sQuery(id+"F0.wireOp",EDGE,"E24.0"),sQuery(id+"F0.wireOp",EDGE,"E25.0"),sQuery(id+"F0.wireOp",EDGE,"E26"),sQuery(id+"F0.wireOp",EDGE,"E27"),sQuery(id+"F0.wireOp",EDGE,"E28"),sQuery(id+"F0.wireOp",EDGE,"E29"),sQuery(id+"F0.wireOp",EDGE,"E30"),sQuery(id+"F0.wireOp",EDGE,"E31"),sQuery(id+"F0.wireOp",EDGE,"E32"),sQuery(id+"F0.wireOp",EDGE,"E33"),sQuery(id+"F0.wireOp",EDGE,"E34"),sQuery(id+"F0.wireOp",EDGE,"E35"),sQuery(id+"F0.wireOp",EDGE,"E36"),sQuery(id+"F0.wireOp",EDGE,"E37"),sQuery(id+"F0.wireOp",EDGE,"E38"),sQuery(id+"F0.wireOp",EDGE,"E39"),sQuery(id+"F0.wireOp",EDGE,"E40"),sQuery(id+"F0.wireOp",EDGE,"E41"),sQuery(id+"F0.wireOp",EDGE,"E42"),sQuery(id+"F0.wireOp",EDGE,"E43"),sQuery(id+"F0.wireOp",EDGE,"E44"),sQuery(id+"F0.wireOp",EDGE,"E45"),sQuery(id+"F0.wireOp",EDGE,"E46"),sQuery(id+"F0.wireOp",EDGE,"E48.trimOffspring"),sQuery(id+"F0.wireOp",EDGE,"E49.trimOffspring"),sQuery(id+"F0.wireOp",EDGE,"E50.trimOffspring"),sQuery(id+"F0.wireOp",EDGE,"E51.trimOffspring"),sQuery(id+"F0.wireOp",EDGE,"E52.trimOffspring"),sQuery(id+"F0.wireOp",EDGE,"E53.trimOffspring"),sQuery(id+"F0.wireOp",EDGE,"E54.trimOffspring"),sQuery(id+"F0.wireOp",EDGE,"E55.trimOffspring"),sQuery(id+"F0.wireOp",EDGE,"E56.trimOffspring"),sQuery(id+"F0.wireOp",EDGE,"E57.trimOffspring"),sQuery(id+"F0.wireOp",EDGE,"E58.trimOffspring"),sQuery(id+"F0.wireOp",EDGE,"E59.trimOffspring"),sQuery(id+"F0.wireOp",EDGE,"E60.trimOffspring"),sQuery(id+"F0.wireOp",EDGE,"E61.trimOffspring"),sQuery(id+"F0.wireOp",EDGE,"E62.trimOffspring"),sQuery(id+"F0.wireOp",EDGE,"E63.trimOffspring"),sQuery(id+"F0.wireOp",EDGE,"E64.trimOffspring"),sQuery(id+"F0.wireOp",EDGE,"E65.trimOffspring"),sQuery(id+"F0.wireOp",EDGE,"E66.trimOffspring"),sQuery(id+"F0.wireOp",EDGE,"E67.trimOffspring"),sQuery(id+"F0.wireOp",EDGE,"E68.trimOffspring"),sQuery(id+"F0.wireOp",EDGE,"E69.trimOffspring"),sQuery(id+"F0.wireOp",EDGE,"E70.trimOffspring"),sQuery(id+"F0.wireOp",EDGE,"E71.trimOffspring"),sQuery(id+"F0.wireOp",EDGE,"E72.trimOffspring"),sQuery(id+"F0.wireOp",EDGE,"E73.trimOffspring"),sQuery(id+"F0.wireOp",EDGE,"E74.trimOffspring"),sQuery(id+"F0.wireOp",EDGE,"E75.trimOffspring"),sQuery(id+"F0.wireOp",EDGE,"E76.trimOffspring"),sQuery(id+"F0.wireOp",EDGE,"E77.trimOffspring"),sQuery(id+"F0.wireOp",EDGE,"E78.trimOffspring"),sQuery(id+"F0.wireOp",EDGE,"E79.trimOffspring"),sQuery(id+"F0.wireOp",EDGE,"E80.trimOffspring"),sQuery(id+"F0.wireOp",EDGE,"E81.trimOffspring"),sQuery(id+"F0.wireOp",EDGE,"E82.trimOffspring"),sQuery(id+"F0.wireOp",EDGE,"E83.trimOffspring"),sQuery(id+"F0.wireOp",EDGE,"E84.trimOffspring"),sQuery(id+"F0.wireOp",EDGE,"E85.trimOffspring"),sQuery(id+"F0.wireOp",EDGE,"E86.trimOffspring"),sQuery(id+"F0.wireOp",EDGE,"E87.trimOffspring"),sQuery(id+"F0.wireOp",EDGE,"E88.trimOffspring"),sQuery(id+"F0.wireOp",EDGE,"E89.trimOffspring"),sQuery(id+"F0.wireOp",EDGE,"E90.trimOffspring"),sQuery(id+"F0.wireOp",EDGE,"E91.trimOffspring"),sQuery(id+"F0.wireOp",EDGE,"E92.trimOffspring"),sQuery(id+"F0.wireOp",EDGE,"E93.trimOffspring"),sQuery(id+"F0.wireOp",EDGE,"E94.trimOffspring"),sQuery(id+"F0.wireOp",EDGE,"E95.trimOffspring"),sQuery(id+"F0.wireOp",EDGE,"E96.trimOffspring"),sQuery(id+"F0.wireOp",EDGE,"E97.trimOffspring"),sQuery(id+"F0.wireOp",EDGE,"E98.trimOffspring"),sQuery(id+"F0.wireOp",EDGE,"E99.trimOffspring"),sQuery(id+"F0.wireOp",EDGE,"E100.trimOffspring"),sQuery(id+"F0.wireOp",EDGE,"E101.trimOffspring"),sQuery(id+"F0.wireOp",EDGE,"E102"),sQuery(id+"F0.wireOp",EDGE,"E103"),sQuery(id+"F0.wireOp",EDGE,"E104"),sQuery(id+"F0.wireOp",EDGE,"E105"),sQuery(id+"F0.wireOp",EDGE,"E106"),sQuery(id+"F0.wireOp",EDGE,"E107"),sQuery(id+"F0.wireOp",EDGE,"E108"),sQuery(id+"F0.wireOp",EDGE,"E109"),sQuery(id+"F0.wireOp",EDGE,"E110"),sQuery(id+"F0.wireOp",EDGE,"E111"),sQuery(id+"F0.wireOp",EDGE,"E112"),sQuery(id+"F0.wireOp",EDGE,"E113"),sQuery(id+"F0.wireOp",EDGE,"E114"),sQuery(id+"F0.wireOp",EDGE,"E115"),sQuery(id+"F0.wireOp",EDGE,"E116"),sQuery(id+"F0.wireOp",EDGE,"E117"),sQuery(id+"F0.wireOp",EDGE,"E118.MirrorCS"),sQuery(id+"F0.wireOp",EDGE,"E119.MirrorCS"),sQuery(id+"F0.wireOp",EDGE,"E120.MirrorCS"),sQuery(id+"F0.wireOp",EDGE,"E121.MirrorCS"),sQuery(id+"F0.wireOp",EDGE,"E122.MirrorCS"),sQuery(id+"F0.wireOp",EDGE,"E123.MirrorCS"),sQuery(id+"F0.wireOp",EDGE,"E124.MirrorCS"),sQuery(id+"F0.wireOp",EDGE,"E125.MirrorCS"),sQuery(id+"F0.wireOp",EDGE,"E126.MirrorCS"),sQuery(id+"F0.wireOp",EDGE,"E127.MirrorCS"),sQuery(id+"F0.wireOp",EDGE,"E128.MirrorCS"),sQuery(id+"F0.wireOp",EDGE,"E129.MirrorCS"),sQuery(id+"F0.wireOp",EDGE,"E130.1.0"),sQuery(id+"F0.wireOp",EDGE,"E130.1.1"),sQuery(id+"F0.wireOp",EDGE,"E130.1.2"),sQuery(id+"F0.wireOp",EDGE,"E130.1.3"),sQuery(id+"F0.wireOp",EDGE,"E130.1.4"),sQuery(id+"F0.wireOp",EDGE,"E130.1.5"),sQuery(id+"F0.wireOp",EDGE,"E130.1.6"),sQuery(id+"F0.wireOp",EDGE,"E130.1.7"),sQuery(id+"F0.wireOp",EDGE,"E130.1.8"),sQuery(id+"F0.wireOp",EDGE,"E130.1.9"),sQuery(id+"F0.wireOp",EDGE,"E130.1.10"),sQuery(id+"F0.wireOp",EDGE,"E130.1.11"),sQuery(id+"F0.wireOp",EDGE,"E130.1.12"),sQuery(id+"F0.wireOp",EDGE,"E130.1.13"),sQuery(id+"F0.wireOp",EDGE,"E130.1.14"),sQuery(id+"F0.wireOp",EDGE,"E130.1.15"),sQuery(id+"F0.wireOp",EDGE,"E130.1.16"),sQuery(id+"F0.wireOp",EDGE,"E130.1.17"),sQuery(id+"F0.wireOp",EDGE,"E130.1.18"),sQuery(id+"F0.wireOp",EDGE,"E130.1.19"),sQuery(id+"F0.wireOp",EDGE,"E130.1.20"),sQuery(id+"F0.wireOp",EDGE,"E130.1.21"),sQuery(id+"F0.wireOp",EDGE,"E130.1.22"),sQuery(id+"F0.wireOp",EDGE,"E130.1.23"),sQuery(id+"F0.wireOp",EDGE,"E130.2.0"),sQuery(id+"F0.wireOp",EDGE,"E130.2.1"),sQuery(id+"F0.wireOp",EDGE,"E130.2.2"),sQuery(id+"F0.wireOp",EDGE,"E130.2.3"),sQuery(id+"F0.wireOp",EDGE,"E130.2.4"),sQuery(id+"F0.wireOp",EDGE,"E130.2.5"),sQuery(id+"F0.wireOp",EDGE,"E130.2.6"),sQuery(id+"F0.wireOp",EDGE,"E130.2.7"),sQuery(id+"F0.wireOp",EDGE,"E130.2.8"),sQuery(id+"F0.wireOp",EDGE,"E130.2.9"),sQuery(id+"F0.wireOp",EDGE,"E130.2.10"),sQuery(id+"F0.wireOp",EDGE,"E130.2.11"),sQuery(id+"F0.wireOp",EDGE,"E130.2.12"),sQuery(id+"F0.wireOp",EDGE,"E130.2.13"),sQuery(id+"F0.wireOp",EDGE,"E130.2.14"),sQuery(id+"F0.wireOp",EDGE,"E130.2.15"),sQuery(id+"F0.wireOp",EDGE,"E130.2.16"),sQuery(id+"F0.wireOp",EDGE,"E130.2.17"),sQuery(id+"F0.wireOp",EDGE,"E130.2.18"),sQuery(id+"F0.wireOp",EDGE,"E130.2.19"),sQuery(id+"F0.wireOp",EDGE,"E130.2.20"),sQuery(id+"F0.wireOp",EDGE,"E130.2.21"),sQuery(id+"F0.wireOp",EDGE,"E130.2.22"),sQuery(id+"F0.wireOp",EDGE,"E130.2.23"),sQuery(id+"F0.wireOp",EDGE,"E130.3.0"),sQuery(id+"F0.wireOp",EDGE,"E130.3.1"),sQuery(id+"F0.wireOp",EDGE,"E130.3.2"),sQuery(id+"F0.wireOp",EDGE,"E130.3.3"),sQuery(id+"F0.wireOp",EDGE,"E130.3.4"),sQuery(id+"F0.wireOp",EDGE,"E130.3.5"),sQuery(id+"F0.wireOp",EDGE,"E130.3.6"),sQuery(id+"F0.wireOp",EDGE,"E130.3.7"),sQuery(id+"F0.wireOp",EDGE,"E130.3.8"),sQuery(id+"F0.wireOp",EDGE,"E130.3.9"),sQuery(id+"F0.wireOp",EDGE,"E130.3.10"),sQuery(id+"F0.wireOp",EDGE,"E130.3.11"),sQuery(id+"F0.wireOp",EDGE,"E130.3.12"),sQuery(id+"F0.wireOp",EDGE,"E130.3.13"),sQuery(id+"F0.wireOp",EDGE,"E130.3.14"),sQuery(id+"F0.wireOp",EDGE,"E130.3.15"),sQuery(id+"F0.wireOp",EDGE,"E130.3.16"),sQuery(id+"F0.wireOp",EDGE,"E130.3.17"),sQuery(id+"F0.wireOp",EDGE,"E130.3.18"),sQuery(id+"F0.wireOp",EDGE,"E130.3.19"),sQuery(id+"F0.wireOp",EDGE,"E130.3.20"),sQuery(id+"F0.wireOp",EDGE,"E130.3.21"),sQuery(id+"F0.wireOp",EDGE,"E130.3.22"),sQuery(id+"F0.wireOp",EDGE,"E130.3.23"),sQuery(id+"F0.wireOp",EDGE,"E130.4.0"),sQuery(id+"F0.wireOp",EDGE,"E130.4.1"),sQuery(id+"F0.wireOp",EDGE,"E130.4.2"),sQuery(id+"F0.wireOp",EDGE,"E130.4.3"),sQuery(id+"F0.wireOp",EDGE,"E130.4.4"),sQuery(id+"F0.wireOp",EDGE,"E130.4.5"),sQuery(id+"F0.wireOp",EDGE,"E130.4.6"),sQuery(id+"F0.wireOp",EDGE,"E130.4.7"),sQuery(id+"F0.wireOp",EDGE,"E130.4.8"),sQuery(id+"F0.wireOp",EDGE,"E130.4.9"),sQuery(id+"F0.wireOp",EDGE,"E130.4.10"),sQuery(id+"F0.wireOp",EDGE,"E130.4.11"),sQuery(id+"F0.wireOp",EDGE,"E130.4.12"),sQuery(id+"F0.wireOp",EDGE,"E130.4.13"),sQuery(id+"F0.wireOp",EDGE,"E130.4.14"),sQuery(id+"F0.wireOp",EDGE,"E130.4.15"),sQuery(id+"F0.wireOp",EDGE,"E130.4.16"),sQuery(id+"F0.wireOp",EDGE,"E130.4.17"),sQuery(id+"F0.wireOp",EDGE,"E130.4.18"),sQuery(id+"F0.wireOp",EDGE,"E130.4.19"),sQuery(id+"F0.wireOp",EDGE,"E130.4.20"),sQuery(id+"F0.wireOp",EDGE,"E130.4.21"),sQuery(id+"F0.wireOp",EDGE,"E130.4.22"),sQuery(id+"F0.wireOp",EDGE,"E130.4.23"),sQuery(id+"F0.wireOp",EDGE,"E130.5.0"),sQuery(id+"F0.wireOp",EDGE,"E130.5.1"),sQuery(id+"F0.wireOp",EDGE,"E130.5.2"),sQuery(id+"F0.wireOp",EDGE,"E130.5.3"),sQuery(id+"F0.wireOp",EDGE,"E130.5.4"),sQuery(id+"F0.wireOp",EDGE,"E130.5.5"),sQuery(id+"F0.wireOp",EDGE,"E130.5.6"),sQuery(id+"F0.wireOp",EDGE,"E130.5.7"),sQuery(id+"F0.wireOp",EDGE,"E130.5.8"),sQuery(id+"F0.wireOp",EDGE,"E130.5.9"),sQuery(id+"F0.wireOp",EDGE,"E130.5.10"),sQuery(id+"F0.wireOp",EDGE,"E130.5.11"),sQuery(id+"F0.wireOp",EDGE,"E130.5.12"),sQuery(id+"F0.wireOp",EDGE,"E130.5.13"),sQuery(id+"F0.wireOp",EDGE,"E130.5.14"),sQuery(id+"F0.wireOp",EDGE,"E130.5.15"),sQuery(id+"F0.wireOp",EDGE,"E130.5.16"),sQuery(id+"F0.wireOp",EDGE,"E130.5.17"),sQuery(id+"F0.wireOp",EDGE,"E130.5.18"),sQuery(id+"F0.wireOp",EDGE,"E130.5.19"),sQuery(id+"F0.wireOp",EDGE,"E130.5.20"),sQuery(id+"F0.wireOp",EDGE,"E130.5.21"),sQuery(id+"F0.wireOp",EDGE,"E130.5.22"),sQuery(id+"F0.wireOp",EDGE,"E130.5.23"),sQuery(id+"F0.wireOp",EDGE,"E130.6.0"),sQuery(id+"F0.wireOp",EDGE,"E130.6.1"),sQuery(id+"F0.wireOp",EDGE,"E130.6.2"),sQuery(id+"F0.wireOp",EDGE,"E130.6.3"),sQuery(id+"F0.wireOp",EDGE,"E130.6.4"),sQuery(id+"F0.wireOp",EDGE,"E130.6.5"),sQuery(id+"F0.wireOp",EDGE,"E130.6.6"),sQuery(id+"F0.wireOp",EDGE,"E130.6.7"),sQuery(id+"F0.wireOp",EDGE,"E130.6.8"),sQuery(id+"F0.wireOp",EDGE,"E130.6.9"),sQuery(id+"F0.wireOp",EDGE,"E130.6.10"),sQuery(id+"F0.wireOp",EDGE,"E130.6.11"),sQuery(id+"F0.wireOp",EDGE,"E130.6.12"),sQuery(id+"F0.wireOp",EDGE,"E130.6.13"),sQuery(id+"F0.wireOp",EDGE,"E130.6.14"),sQuery(id+"F0.wireOp",EDGE,"E130.6.15"),sQuery(id+"F0.wireOp",EDGE,"E130.6.16"),sQuery(id+"F0.wireOp",EDGE,"E130.6.17"),sQuery(id+"F0.wireOp",EDGE,"E130.6.18"),sQuery(id+"F0.wireOp",EDGE,"E130.6.19"),sQuery(id+"F0.wireOp",EDGE,"E130.6.20"),sQuery(id+"F0.wireOp",EDGE,"E130.6.21"),sQuery(id+"F0.wireOp",EDGE,"E130.6.22"),sQuery(id+"F0.wireOp",EDGE,"E130.6.23")])],"isStart":false}),makeQuery(id+"F3.opExtrude","CAP_FACE",FACE,{"disambiguationData":[OSD([sQuery(id+"F2.wireOp",EDGE,"E131.0"),sQuery(id+"F2.wireOp",EDGE,"E141.6.0"),sQuery(id+"F2.wireOp",EDGE,"E141.6.1")])],"isStart":false}),makeQuery(id+"F3.opExtrude","CAP_FACE",FACE,{"disambiguationData":[OSD([sQuery(id+"F2.wireOp",EDGE,"E132.0"),sQuery(id+"F2.wireOp",EDGE,"E141.5.0"),sQuery(id+"F2.wireOp",EDGE,"E141.5.1"),sQuery(id+"F2.wireOp",EDGE,"E142")])],"isStart":false}),makeQuery(id+"F3.opExtrude","CAP_FACE",FACE,{"disambiguationData":[OSD([sQuery(id+"F2.wireOp",EDGE,"E133.0"),sQuery(id+"F2.wireOp",EDGE,"E141.4.0"),sQuery(id+"F2.wireOp",EDGE,"E141.4.1")])],"isStart":false}),makeQuery(id+"F3.opExtrude","CAP_FACE",FACE,{"disambiguationData":[OSD([sQuery(id+"F2.wireOp",EDGE,"E134.0"),sQuery(id+"F2.wireOp",EDGE,"E141.3.0"),sQuery(id+"F2.wireOp",EDGE,"E141.3.1")])],"isStart":false}),makeQuery(id+"F3.opExtrude","CAP_FACE",FACE,{"disambiguationData":[OSD([sQuery(id+"F2.wireOp",EDGE,"E135.0"),sQuery(id+"F2.wireOp",EDGE,"E141.2.0"),sQuery(id+"F2.wireOp",EDGE,"E141.2.1")])],"isStart":false}),makeQuery(id+"F3.opExtrude","CAP_FACE",FACE,{"disambiguationData":[OSD([sQuery(id+"F2.wireOp",EDGE,"E136.0"),sQuery(id+"F2.wireOp",EDGE,"E141.1.0"),sQuery(id+"F2.wireOp",EDGE,"E141.1.1")])],"isStart":false}),makeQuery(id+"F3.opExtrude","CAP_FACE",FACE,{"disambiguationData":[OSD([sQuery(id+"F2.wireOp",EDGE,"E137.0"),sQuery(id+"F2.wireOp",EDGE,"E139"),sQuery(id+"F2.wireOp",EDGE,"E140")])],"isStart":false})]});
            var sketch = newSketch(context, id + "F4", { "sketchPlane" : qUnion([Q0])});
            skText(sketch, "E143", { "text": "Baby\'s First \n Christmas\n  \n    Nicky G.\n       2016", "fontName": "NotoSerif-BoldItalic.ttf"});
            const initialGuessF4  = {"E143": [-0.0428, 0.0297, 1, 0, 0.01]};
            skSetInitialGuess(sketch, initialGuessF4);
            skSolve(sketch);
        }
        {
            var Q0;
            Q0 = qSketchRegion(id + "F4", true);
            var Q1;
            Q1 = qConstructionFilter(qBodyType(qCreatedBy(id + "F4" ,EDGE), BodyType.WIRE), ConstructionObject.NO);
            extrude(context, id + "F5", {"entities" : qUnion([Q0]), "operationType" : NewBodyOperationType.ADD, "surfaceEntities" : qUnion([Q1]), "depth" : 3 * mm});
        }
    });
